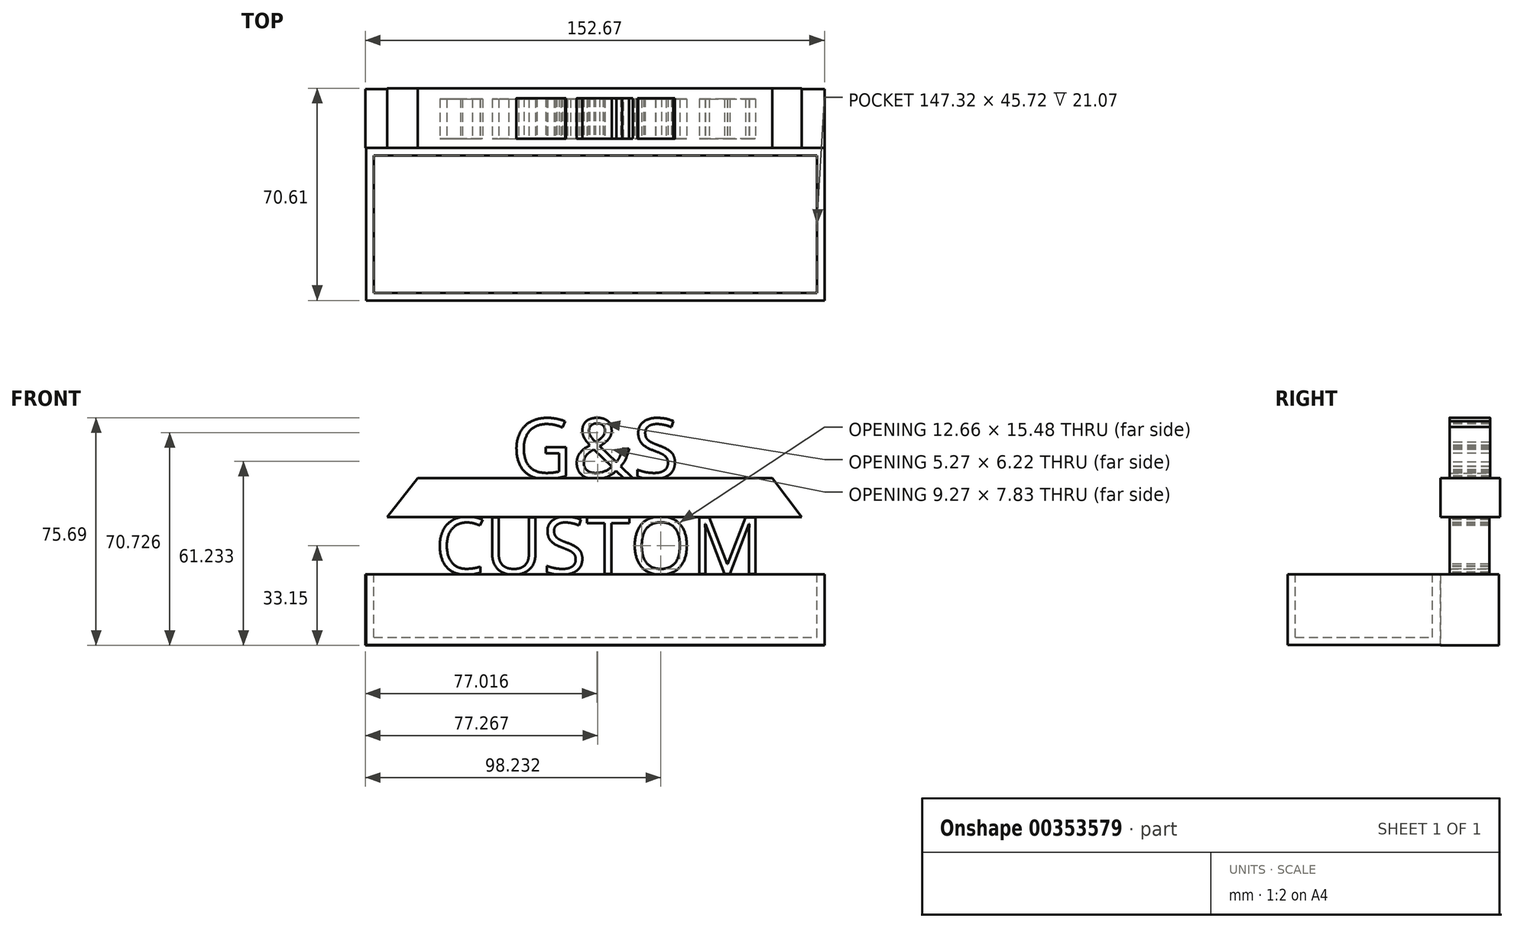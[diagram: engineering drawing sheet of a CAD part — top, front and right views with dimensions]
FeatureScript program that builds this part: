
annotation { "Feature Type Name" : "Feature", "Feature Type Description" : "" }
export const myFeature = defineFeature(function(context is Context, id is Id, definition is map)
    precondition{}
    {
        {
            var Q0;
            Q0=qCreatedBy(makeId("Front.planeOp"),FACE);
            var sketch = newSketch(context, id + "F0", { "sketchPlane" : qUnion([Q0])});
            skLineSegment(sketch, "E0", {"start": v(-51.55, -35.7) * mm, "end": v(100.85, -35.7) * mm});
            skLineSegment(sketch, "E1", {"start": v(100.85, -35.7) * mm, "end": v(100.85, -12.1) * mm});
            skLineSegment(sketch, "E2", {"start": v(-51.55, -35.7) * mm, "end": v(-51.55, -12.1) * mm});
            skLineSegment(sketch, "E3", {"start": v(-51.55, -12.1) * mm, "end": v(100.85, -12.1) * mm});
            skSolve(sketch);
        }
        {
            var Q0;
            Q0 = qSketchRegion(id + "F0", true);
            extrude(context, id + "F1", {"entities" : qUnion([Q0]), "depth" : 50.8 * mm});
        }
        {
            var Q0;
            Q0=makeQuery(id+"F1.opExtrude","SWEPT_FACE",FACE,{"disambiguationData":[OSD([sQuery(id+"F0.wireOp",EDGE,"ZqYcZAaT-oN1F-vEPQ-wBBI-WomqK9GeIlas.top")])]});
            var Q1;
            Q1=makeQuery(id+"F1.opExtrude","SWEPT_FACE",FACE,{"disambiguationData":[OSD([sQuery(id+"F0.wireOp",EDGE,"E3")])]});
            shell(context, id + "F2", {"entities" : qUnion([Q0, Q1]), "thickness" : 2.54 * mm});
        }
        {
            var Q0;
            Q0=qCreatedBy(makeId("Right.planeOp"),FACE);
            var sketch = newSketch(context, id + "F3", { "sketchPlane" : qUnion([Q0])});
            skLineSegment(sketch, "E4.bottom", {"start": v(0, -12.16) * mm, "end": v(19.53, -12.16) * mm});
            skLineSegment(sketch, "E4.top", {"start": v(0, -35.77) * mm, "end": v(19.53, -35.77) * mm});
            skLineSegment(sketch, "E4.left", {"start": v(0, -12.16) * mm, "end": v(0, -35.77) * mm});
            skLineSegment(sketch, "E4.right", {"start": v(19.53, -12.16) * mm, "end": v(19.53, -35.77) * mm});
            skSolve(sketch);
        }
        {
            var Q0;
            Q0 = qSketchRegion(id + "F3", true);
            extrude(context, id + "F4", {"entities" : qUnion([Q0]), "operationType" : NewBodyOperationType.ADD, "depth" : 100.84 * mm, "hasSecondDirection" : true, "secondDirectionOppositeDirection" : true, "secondDirectionDepth" : 51.82 * mm});
        }
        {
            var Q0;
            Q0=qCreatedBy(makeId("Front.planeOp"),FACE);
            var sketch = newSketch(context, id + "F5", { "sketchPlane" : qUnion([Q0])});
            skText(sketch, "E5", { "text": "CUSTOM", "fontName": "OpenSans-Regular.ttf"});
            const initialGuessF5  = {"E5": [-0.02865, -0.01202, 1, 0, 0.01896]};
            skSetInitialGuess(sketch, initialGuessF5);
            skSolve(sketch);
        }
        {
            var Q0;
            Q0 = qSketchRegion(id + "F5", true);
            extrude(context, id + "F6", {"entities" : qUnion([Q0]), "operationType" : NewBodyOperationType.ADD, "oppositeDirection" : true, "depth" : 16.26 * mm, "hasSecondDirection" : true, "secondDirectionOppositeDirection" : true, "secondDirectionDepth" : 3.05 * mm});
        }
        {
            var Q0;
            Q0=qCreatedBy(makeId("Front.planeOp"),FACE);
            var sketch = newSketch(context, id + "F7", { "sketchPlane" : qUnion([Q0])});
            skLineSegment(sketch, "E6", {"start": v(-44.56, 6.94) * mm, "end": v(93.25, 6.94) * mm});
            skLineSegment(sketch, "E7", {"start": v(-44.56, 6.94) * mm, "end": v(-34.4, 19.8) * mm});
            skLineSegment(sketch, "E8", {"start": v(93.25, 6.94) * mm, "end": v(83.43, 19.8) * mm});
            skLineSegment(sketch, "E9", {"start": v(-34.4, 19.8) * mm, "end": v(83.43, 19.8) * mm});
            skSolve(sketch);
        }
        {
            var Q0;
            Q0 = qSketchRegion(id + "F7", true);
            extrude(context, id + "F8", {"entities" : qUnion([Q0]), "operationType" : NewBodyOperationType.ADD, "oppositeDirection" : true, "depth" : 19.8 * mm, "hasSecondDirection" : true, "secondDirectionOppositeDirection" : false, "secondDirectionDepth" : 0 * mm});
        }
        {
            var Q0;
            Q0=qCreatedBy(makeId("Front.planeOp"),FACE);
            var sketch = newSketch(context, id + "F9", { "sketchPlane" : qUnion([Q0])});
            skText(sketch, "E10", { "text": "G&S", "fontName": "OpenSans-Regular.ttf"});
            const initialGuessF9  = {"E10": [-0.00325, 0.0198, 1, 0, 0.01998]};
            skSetInitialGuess(sketch, initialGuessF9);
            skSolve(sketch);
        }
        {
            var Q0;
            Q0 = qSketchRegion(id + "F9", true);
            extrude(context, id + "F10", {"entities" : qUnion([Q0]), "operationType" : NewBodyOperationType.ADD, "oppositeDirection" : true, "depth" : 16.5 * mm, "hasSecondDirection" : true, "secondDirectionOppositeDirection" : true, "secondDirectionDepth" : 3.05 * mm});
        }
        {
            var Q0;
            Q0=makeQuery(id+"F6.opExtrude","CAP_FACE",FACE,{"disambiguationData":[OSD([sQuery(id+"F5.wireOp",EDGE,"E5.sketch_text.stroke-54"),sQuery(id+"F5.wireOp",EDGE,"E5.sketch_text.stroke-55"),sQuery(id+"F5.wireOp",EDGE,"E5.sketch_text.stroke-56"),sQuery(id+"F5.wireOp",EDGE,"E5.sketch_text.stroke-57"),sQuery(id+"F5.wireOp",EDGE,"E5.sketch_text.stroke-58"),sQuery(id+"F5.wireOp",EDGE,"E5.sketch_text.stroke-59"),sQuery(id+"F5.wireOp",EDGE,"E5.sketch_text.stroke-60"),sQuery(id+"F5.wireOp",EDGE,"E5.sketch_text.stroke-61")])],"isStart":true});
            var sketch = newSketch(context, id + "F11", { "sketchPlane" : qUnion([Q0])});
            skLineSegment(sketch, "E11.bottom", {"start": v(27.78, -12.02) * mm, "end": v(29.97, -12.02) * mm});
            skLineSegment(sketch, "E11.top", {"start": v(27.78, -12.2) * mm, "end": v(29.97, -12.2) * mm});
            skLineSegment(sketch, "E11.left", {"start": v(27.78, -12.02) * mm, "end": v(27.78, -12.2) * mm});
            skLineSegment(sketch, "E11.right", {"start": v(29.97, -12.02) * mm, "end": v(29.97, -12.2) * mm});
            skSolve(sketch);
        }
        {
            var Q0;
            Q0 = qSketchRegion(id + "F11", true);
            extrude(context, id + "F12", {"entities" : qUnion([Q0]), "operationType" : NewBodyOperationType.ADD, "oppositeDirection" : true, "depth" : 13.2 * mm, "offsetDistance" : 25.4 * mm});
        }
    });
